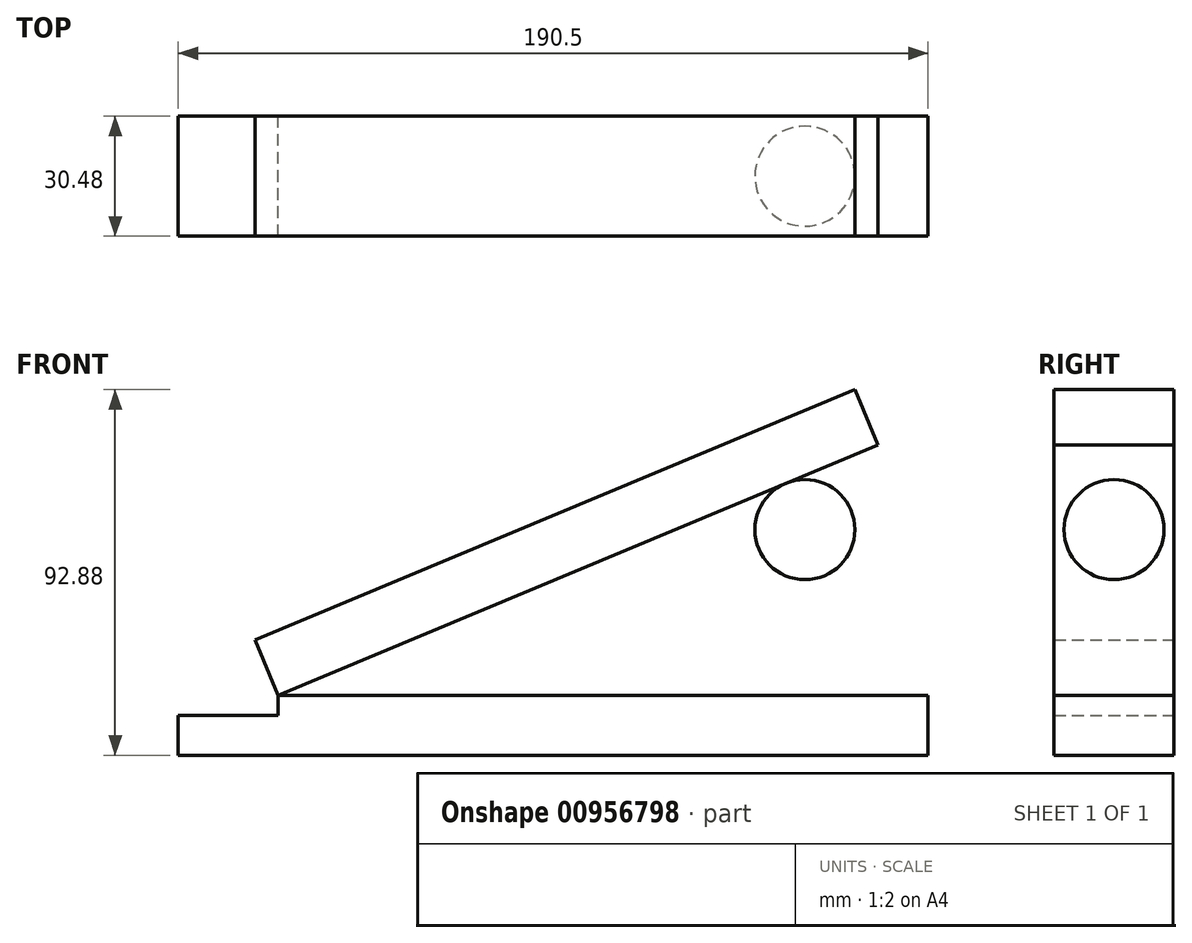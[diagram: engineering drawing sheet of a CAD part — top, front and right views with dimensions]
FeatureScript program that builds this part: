
annotation { "Feature Type Name" : "Feature", "Feature Type Description" : "" }
export const myFeature = defineFeature(function(context is Context, id is Id, definition is map)
    precondition{}
    {
        {
            var Q0;
            Q0=qCreatedBy(makeId("Front.planeOp"),FACE);
            var sketch = newSketch(context, id + "F0", { "sketchPlane" : qUnion([Q0])});
            skLineSegment(sketch, "E0", {"start": v(0, 0) * mm, "end": v(165.1, 0) * mm});
            skLineSegment(sketch, "E1", {"start": v(165.1, 0) * mm, "end": v(165.1, -15.24) * mm});
            skLineSegment(sketch, "E2", {"start": v(165.1, -15.24) * mm, "end": v(-25.4, -15.24) * mm});
            skLineSegment(sketch, "E3", {"start": v(-25.4, -15.24) * mm, "end": v(-25.4, -5.08) * mm});
            skLineSegment(sketch, "E4", {"start": v(-25.4, -5.08) * mm, "end": v(0, -5.08) * mm});
            skLineSegment(sketch, "E5", {"start": v(0, -5.08) * mm, "end": v(0, 0) * mm});
            skLineSegment(sketch, "E6", {"start": v(0, 0) * mm, "end": v(152.37, 63.58) * mm});
            skLineSegment(sketch, "E7", {"start": v(152.37, 63.58) * mm, "end": v(146.5, 77.64) * mm});
            skLineSegment(sketch, "E8", {"start": v(146.5, 77.64) * mm, "end": v(-5.87, 14.06) * mm});
            skLineSegment(sketch, "E9", {"start": v(-5.87, 14.06) * mm, "end": v(0, 0) * mm});
            skArc(sketch, "E10", {"start": v(133.82, 29.38) * mm, "mid": v(146.52, 42.08) * mm, "end": v(133.82, 54.78) * mm});
            skLineSegment(sketch, "E11", {"start": v(133.82, 54.78) * mm, "end": v(133.82, 29.38) * mm});
            skSolve(sketch);
        }
        {
            var Q0;
            Q0=makeQuery(id+"F0.imprint","IMPRINT",FACE,{"disambiguationData":[TD([[makeQuery(id+"F0.imprint","IMPRINT",EDGE,{"derivedFrom":sQuery(id+"F0.wireOp",EDGE,"E0")}),-1.0]])]});
            extrude(context, id + "F1", {"entities" : qUnion([Q0]), "endBound" : BoundingType.SYMMETRIC, "depth" : 30.48 * mm, "offsetDistance" : 25.4 * mm});
        }
        {
            var Q0;
            Q0=makeQuery(id+"F0.imprint","IMPRINT",FACE,{"disambiguationData":[TD([[makeQuery(id+"F0.imprint","IMPRINT",EDGE,{"derivedFrom":sQuery(id+"F0.wireOp",EDGE,"E6")}),1.0]])]});
            extrude(context, id + "F2", {"entities" : qUnion([Q0]), "endBound" : BoundingType.SYMMETRIC, "depth" : 30.48 * mm, "offsetDistance" : 25.4 * mm});
        }
        {
            var Q0;
            Q0=makeQuery(id+"F0.imprint","IMPRINT",FACE,{"disambiguationData":[TD([[makeQuery(id+"F0.imprint","IMPRINT",EDGE,{"derivedFrom":sQuery(id+"F0.wireOp",EDGE,"E10")}),1.0]])]});
            var Q1;
            Q1=sQuery(id+"F0.wireOp",EDGE,"E11");
            revolve(context, id + "F3", {"operationType" : NewBodyOperationType.ADD, "surfaceOperationType" : NewSurfaceOperationType.NEW, "entities" : qUnion([Q0]), "axis" : qUnion([Q1]), "revolveType" : RevolveType.FULL});
        }
    });
